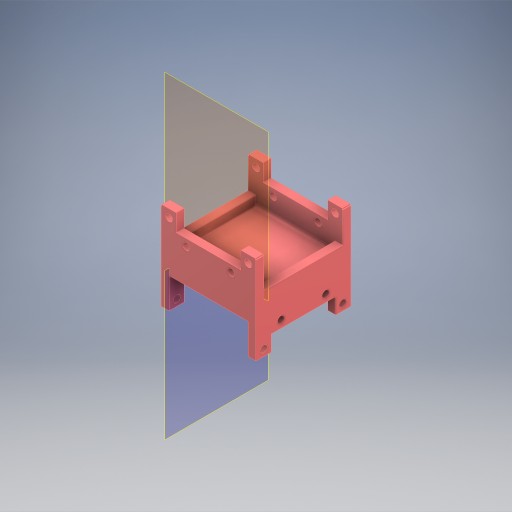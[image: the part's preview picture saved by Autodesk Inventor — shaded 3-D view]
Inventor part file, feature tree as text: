
AUTODESK INVENTOR PART (.ipt)
format: ipt  version: 2024 (Build 280153000, 153)  size: 494,592 bytes
history: native  units: in
note: dims shown in document units (in); Inventor stores cm internally (conversion verified against a paired STEP export)
features: other x7, extrude x6, sketch x6, projected_geometry x6, reference x3, mirror x2, fillet x2
ambient origin geometry x8: Origin, YZ Plane, XZ Plane, XY Plane, X Axis, Y Axis, Z Axis, Center Point
bodies: Body1 (feature_tree)
feature tree (32):
  other  "솔리드2"
  other  "작업 평면2"
  extrude  "돌출2"  Depth=0.0039in
  extrude  "돌출3"  Depth=0.2362in
  mirror  "미러1"
  other  "작업 평면3"
  extrude  "돌출4"  Depth=0.1969in
  extrude  "돌출5"  Depth=0.1969in
  extrude  "돌출6"  Depth=0.1181in TaperAngle=0.0deg
  mirror  "미러4"
  fillet  "모깎기1"  Radius=0.1181in
  extrude  "돌출7"  Depth=0.5906in TaperAngle=0.0deg
  fillet  "모깎기3"  Radius=0.0039in
  sketch  "스케치2"
  reference  "참조2"
  sketch  "스케치4"
  projected_geometry  "투영된 루프2"
  sketch  "스케치5"
  reference  "참조3"
  projected_geometry  "투영된 루프3"
  sketch  "스케치6"
  reference  "참조4"
  projected_geometry  "투영된 루프4"
  projected_geometry  "투영된 루프5"
  sketch  "스케치7"
  projected_geometry  "투영된 루프6"
  sketch  "스케치9"
  projected_geometry  "투영된 루프7"
  other  "조립품1"
  other  "MX-28T_R+idle.ipt:2"
  other  "MX-28T_R:1"
  other  "MX-28T_R+idle.ipt:1"
